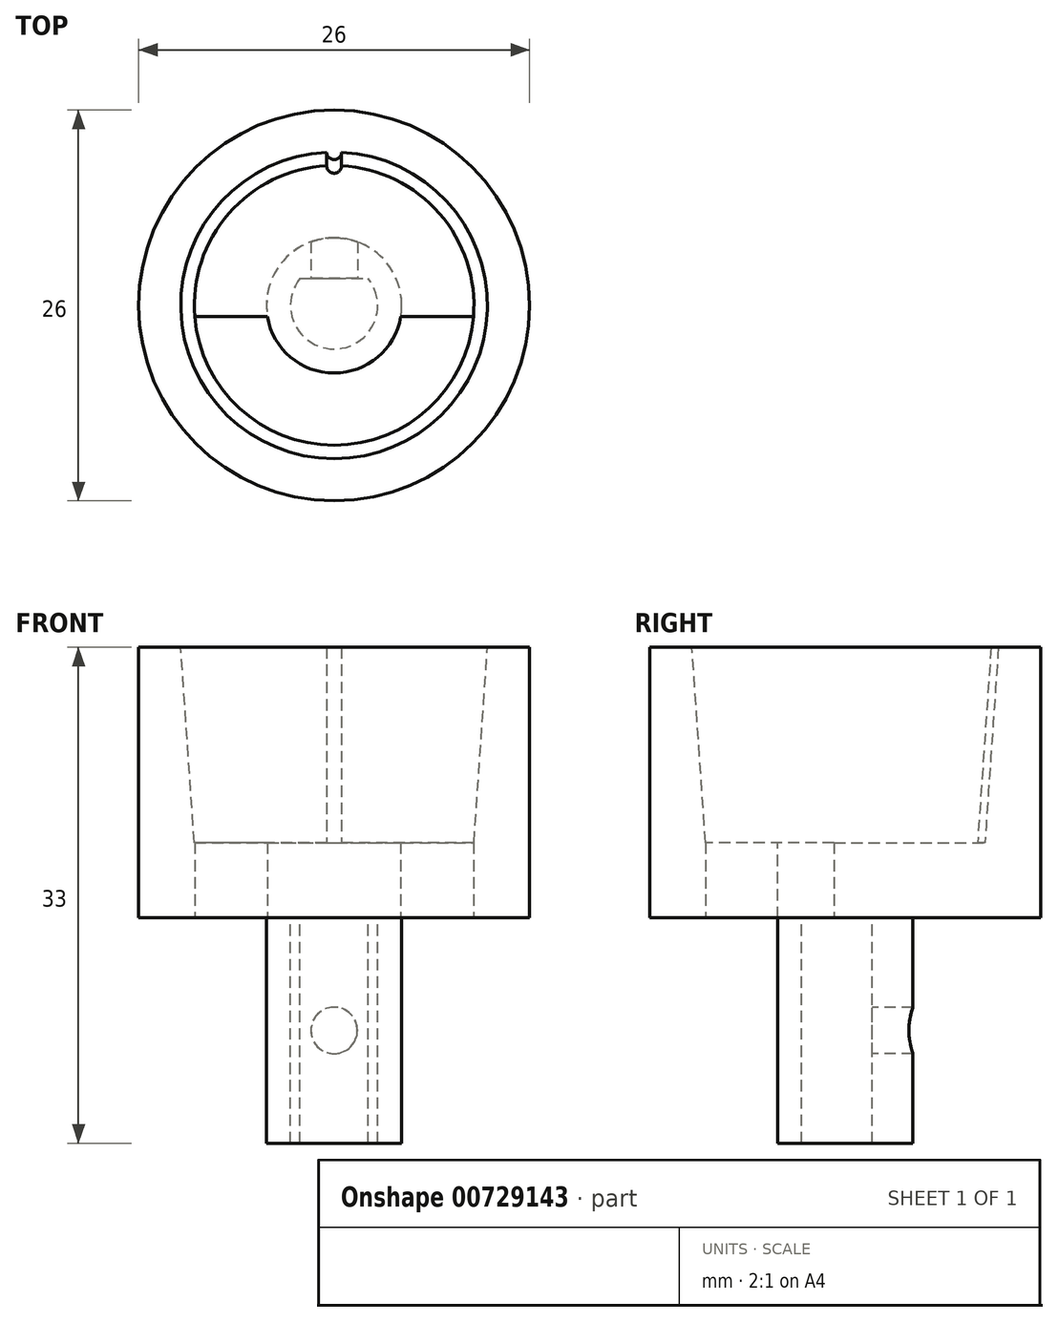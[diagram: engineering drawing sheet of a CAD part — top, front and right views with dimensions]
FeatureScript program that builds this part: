
annotation { "Feature Type Name" : "Feature", "Feature Type Description" : "" }
export const myFeature = defineFeature(function(context is Context, id is Id, definition is map)
    precondition{}
    {
        {
            var Q0;
            Q0=qCreatedBy(makeId("Top.planeOp"),FACE);
            var sketch = newSketch(context, id + "F0", { "sketchPlane" : qUnion([Q0])});
            skCircle(sketch, "E0", {"center": v(0, 0) * mm, "radius": 4.5 * mm});
            skCircle(sketch, "E1", {"center": v(0, 0) * mm, "radius": 10 * mm});
            skArc(sketch, "E2", {"start": v(-2.27, 1.8) * mm, "mid": v(0, -2.9) * mm, "end": v(2.27, 1.8) * mm});
            skLineSegment(sketch, "E3", {"start": v(-2.27, 1.8) * mm, "end": v(2.27, 1.8) * mm});
            skSolve(sketch);
        }
        {
            var Q0;
            Q0=makeQuery(id+"F0.imprint","IMPRINT",FACE,{"disambiguationData":[TD([[makeQuery(id+"F0.imprint","IMPRINT",EDGE,{"derivedFrom":sQuery(id+"F0.wireOp",EDGE,"E0")}),1.0]])]});
            extrude(context, id + "F1", {"entities" : qUnion([Q0]), "oppositeDirection" : true, "depth" : 15 * mm, "offsetDistance" : 25 * mm});
        }
        {
            var Q0;
            Q0=makeQuery(id+"F0.imprint","IMPRINT",FACE,{"disambiguationData":[TD([[makeQuery(id+"F0.imprint","IMPRINT",EDGE,{"derivedFrom":sQuery(id+"F0.wireOp",EDGE,"c1f104ed-909e-43f6-a8f8-68d8a5a1d6da")}),1.0]])]});
            var Q1;
            Q1=makeQuery(id+"F0.imprint","IMPRINT",FACE,{"disambiguationData":[TD([[makeQuery(id+"F0.imprint","IMPRINT",EDGE,{"derivedFrom":sQuery(id+"F0.wireOp",EDGE,"c1f104ed-909e-43f6-a8f8-68d8a5a1d6da")}),-1.0]])]});
            var Q2;
            Q2=makeQuery(id+"F0.imprint","IMPRINT",FACE,{"disambiguationData":[TD([[makeQuery(id+"F0.imprint","IMPRINT",EDGE,{"derivedFrom":sQuery(id+"F0.wireOp",EDGE,"E2")}),1.0]])]});
            var Q3;
            Q3=makeQuery(id+"F0.imprint","IMPRINT",FACE,{"disambiguationData":[TD([[makeQuery(id+"F0.imprint","IMPRINT",EDGE,{"derivedFrom":sQuery(id+"F0.wireOp",EDGE,"E0")}),1.0]])]});
            var Q4;
            Q4=makeQuery(id+"F0.imprint","IMPRINT",FACE,{"disambiguationData":[TD([[makeQuery(id+"F0.imprint","IMPRINT",EDGE,{"derivedFrom":sQuery(id+"F0.wireOp",EDGE,"E0")}),-1.0]])]});
            extrude(context, id + "F2", {"entities" : qUnion([Q0, Q1, Q2, Q3, Q4]), "operationType" : NewBodyOperationType.ADD, "depth" : 5 * mm, "offsetDistance" : 25 * mm});
        }
        {
            var Q0;
            Q0=qCreatedBy(makeId("Right.planeOp"),FACE);
            var sketch = newSketch(context, id + "F3", { "sketchPlane" : qUnion([Q0])});
            skLineSegment(sketch, "E4", {"start": v(9.3, 0) * mm, "end": v(13, 0) * mm});
            skLineSegment(sketch, "E5", {"start": v(13, 0) * mm, "end": v(13, 18) * mm});
            skPoint(sketch, "E6.endSnap0", {"position": v(11.15, 0) * mm});
            skLineSegment(sketch, "E7", {"start": v(9.3, 5) * mm, "end": v(9.3, 0) * mm});
            skLineSegment(sketch, "E8", {"start": v(0, 0) * mm, "end": v(0, 7.26) * mm, "construction": true});
            skLineSegment(sketch, "E9", {"start": v(13, 18) * mm, "end": v(10.2, 18) * mm});
            skLineSegment(sketch, "E10", {"start": v(10.2, 18) * mm, "end": v(9.3, 5) * mm});
            skSolve(sketch);
        }
        {
            var Q0;
            Q0=makeQuery(id+"F3.imprint","IMPRINT",FACE,{"disambiguationData":[TD([[makeQuery(id+"F3.imprint","IMPRINT",EDGE,{"derivedFrom":sQuery(id+"F3.wireOp",EDGE,"E4")}),1.0]])]});
            var Q1;
            Q1=sQuery(id+"F3.wireOp",EDGE,"E8");
            revolve(context, id + "F4", {"operationType" : NewBodyOperationType.ADD, "surfaceOperationType" : NewSurfaceOperationType.NEW, "entities" : qUnion([Q0]), "axis" : qUnion([Q1]), "revolveType" : RevolveType.FULL});
        }
        {
            var Q0;
            Q0=makeQuery(id+"F2.opExtrude","CAP_FACE",FACE,{"disambiguationData":[OSD([sQuery(id+"F0.wireOp",EDGE,"E1")])],"isStart":false});
            var sketch = newSketch(context, id + "F5", { "sketchPlane" : qUnion([Q0])});
            skArc(sketch, "E11", {"start": v(-0.5, 9.29) * mm, "mid": v(0, 8.8) * mm, "end": v(0.5, 9.29) * mm});
            skSolve(sketch);
        }
        {
            var Q0;
            Q0=makeQuery(id+"F4.opRevolve","SWEPT_FACE",FACE,{"disambiguationData":[OSD([sQuery(id+"F3.wireOp",EDGE,"E9")])]});
            var sketch = newSketch(context, id + "F6", { "sketchPlane" : qUnion([Q0])});
            skArc(sketch, "E12", {"start": v(-0.5, 10.19) * mm, "mid": v(0, 9.7) * mm, "end": v(0.5, 10.19) * mm});
            skSolve(sketch);
        }
        {
            var Q1;
            {var subQ0=sQuery(id+"F6.wireOp",EDGE,"E12");Q1=makeQuery(id+"F6.imprint","IMPRINT",FACE,{"disambiguationData":[TD([[makeQuery(id+"F6.imprint","IMPRINT",EDGE,{"derivedFrom":subQ0}),1.0]])]});}
            var Q2;
            {var subQ0=sQuery(id+"F5.wireOp",EDGE,"E11");Q2=makeQuery(id+"F5.imprint","IMPRINT",FACE,{"disambiguationData":[TD([[makeQuery(id+"F5.imprint","IMPRINT",EDGE,{"derivedFrom":subQ0}),1.0]])]});}
            loft(context, id + "F7", {"operationType" : NewBodyOperationType.ADD, "sheetProfilesArray" : [{ "sheetProfileEntities" : qUnion([Q1]) }, { "sheetProfileEntities" : qUnion([Q2]) }]});
        }
        {
            var Q0;
            Q0=makeQuery(id+"F1.opExtrude","SWEPT_FACE",FACE,{"disambiguationData":[OSD([sQuery(id+"F0.wireOp",EDGE,"E3")])]});
            var sketch = newSketch(context, id + "F8", { "sketchPlane" : qUnion([Q0])});
            skPoint(sketch, "E13", {"position": v(0, -7.5) * mm});
            skSolve(sketch);
        }
        {
            var Q0;
            Q0=sQuery(id+"F8.wireOp",VERTEX,"E13");
            var Q1;
            Q1=makeQuery(id+"F1.opExtrude","SWEPT_BODY",BODY,{"disambiguationData":[OSD([sQuery(id+"F0.wireOp",EDGE,"E0"),sQuery(id+"F0.wireOp",EDGE,"E2"),sQuery(id+"F0.wireOp",EDGE,"E3")])]});
            hole(context, id + "F9", {"style" : HoleStyle.SIMPLE, "endStyle" : HoleEndStyle.BLIND, "holeDiameter" : 3.1 * mm, "majorDiameter" : 5 * mm, "holeDepth" : 12 * mm, "isTappedThrough" : true, "tappedDepth" : 12 * mm, "tapClearance" : 3, "locations" : qUnion([Q0]), "scope" : qUnion([Q1])});
        }
        {
            var Q0;
            Q0=makeQuery(id+"F0.imprint","IMPRINT",FACE,{"disambiguationData":[TD([[makeQuery(id+"F0.imprint","IMPRINT",EDGE,{"derivedFrom":sQuery(id+"F0.wireOp",EDGE,"E0")}),-1.0]])]});
            var sketch = newSketch(context, id + "F10", { "sketchPlane" : qUnion([Q0])});
            skCircle(sketch, "E14", {"center": v(0, 0) * mm, "radius": 9.3 * mm});
            skCircle(sketch, "E15", {"center": v(0, 0) * mm, "radius": 4.5 * mm});
            skLineSegment(sketch, "E16", {"start": v(0, 0) * mm, "end": v(9.3, 0) * mm, "construction": true});
            skLineSegment(sketch, "E17", {"start": v(4.44, 0.75) * mm, "end": v(9.27, 0.75) * mm});
            skLineSegment(sketch, "E18", {"start": v(9.27, -0.75) * mm, "end": v(4.44, -0.75) * mm});
            skLineSegment(sketch, "E19", {"start": v(0, 0) * mm, "end": v(-9.3, 0) * mm, "construction": true});
            skLineSegment(sketch, "E20", {"start": v(-4.44, 0.75) * mm, "end": v(-9.27, 0.75) * mm});
            skLineSegment(sketch, "E21", {"start": v(-4.44, -0.75) * mm, "end": v(-9.27, -0.75) * mm});
            skSolve(sketch);
        }
        {
            var Q0;
            {var subQ0=sQuery(id+"F10.wireOp",EDGE,"UNxON7kA-0pfK-1S4r-ztV5-gALaxaQKEJG6");Q0=makeQuery(id+"F10.imprint","IMPRINT",FACE,{"disambiguationData":[TD([[makeQuery(id+"F10.imprint","IMPRINT",EDGE,{"derivedFrom":subQ0}),1.0]])]});}
            var Q1;
            {var subQ0=sQuery(id+"F10.wireOp",EDGE,"w7x52oNp-s0uM-9OuM-NAWl-3KZNwbvfvjdb");Q1=makeQuery(id+"F10.imprint","IMPRINT",FACE,{"disambiguationData":[TD([[makeQuery(id+"F10.imprint","IMPRINT",EDGE,{"derivedFrom":subQ0}),-1.0]])]});}
            var Q2;
            {var subQ0=sQuery(id+"F10.wireOp",EDGE,"E18");Q2=makeQuery(id+"F10.imprint","IMPRINT",FACE,{"disambiguationData":[TD([[makeQuery(id+"F10.imprint","IMPRINT",EDGE,{"derivedFrom":subQ0}),1.0]])]});}
            extrude(context, id + "F11", {"entities" : qUnion([Q0, Q1, Q2]), "operationType" : NewBodyOperationType.REMOVE, "depth" : 5 * mm, "offsetDistance" : 25 * mm});
        }
    });
